# Revit family: ArandelaConcreto_AEC2W-R_PowerLume
name_source: partatom
category: Luminárias
units: mm (PartAtom-declared; Revit-internal decimal feet)

## family parameters
Compartilhado = Sim
Corte com vazios quando carregada = Sim
Cota do conector redondo = Utilizar diâmetro
Fonte luminosa = Não
Hospedeiro = Face
Manter orientação da anotação = Não
Número OmniClass = 23.80.70.14.11.17
Ponto de cálculo do ambiente = Não
Tipo de parte = Normal
Título OmniClass = Wall or Ceiling Mounted External Lighting

## types (1)
- AEC2W-R
    Base = Metal - Alumínio
    Carga Aparente Luminária = 0 VA
    Catálogo de produtos = https://www.powerlume.com.br
    Comentários de voltagem = 110 ou 220Vac 50/60Hz com driver incorporado
    Contato do fabricante = (54) 3066-6488
    Data da atualização = 27/02/2025
    Descrição = Balizador de embutir LED em concreto
    Difusor = PMMA Injetado transparente anti UV
    Diâmetro do frame = 120 mm  [stored 0.393701 ft]
    Elevação-padrão = 1219 mm
    Fabricante = Power Lume
    Fator de Potência Luminária = 1
    Fluxo luminoso = 221 lm
    Frame = Concreto, leve
    IP = 65
    IRC = 85
    IfcExportAs = IfcLightFixtureType
    Localização = Caxias do Sul - RS / Brasil
    Lâmpada = Placa LED
    Modelo = AEC2W-R
    Peso = 0
    Potência = 2W
    Profundidade = 56 mm  [stored 0.183727 ft]
    Temperatura de cor = 3000K
    Tipo de imagem = FOTO AEC2W-R.png
    URL = https://www.powerlume.com.br
    URL do produto = https://www.powerlume.com.br
    Versão = 1
    Vida útil = 60000h
    Voltagem Luminária = 0 V
    Ângulo de abertura = Assimétrico

note: [stored X ft] marks values corroborated as IEEE doubles in the binary element streams (Revit-internal decimal feet)
